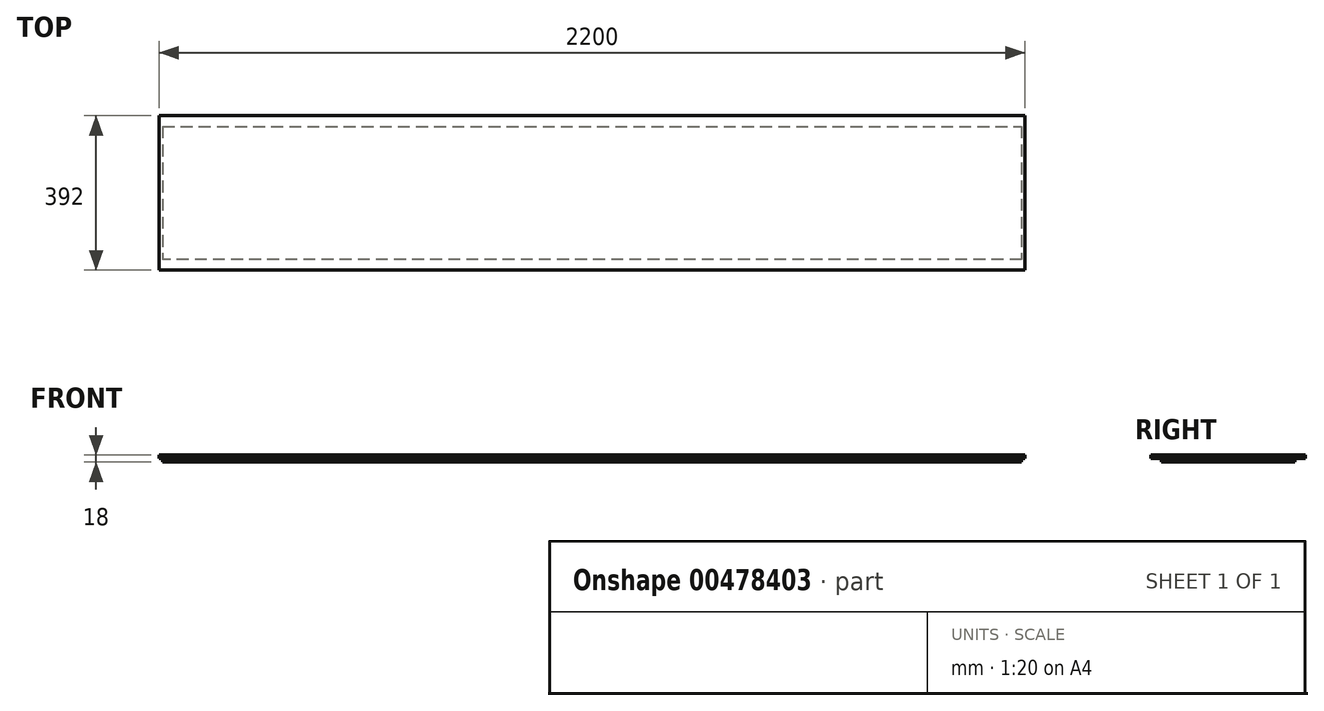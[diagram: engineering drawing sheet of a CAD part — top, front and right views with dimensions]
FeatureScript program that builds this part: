
annotation { "Feature Type Name" : "Feature", "Feature Type Description" : "" }
export const myFeature = defineFeature(function(context is Context, id is Id, definition is map)
    precondition{}
    {
        {
            var Q0;
            Q0=qCreatedBy(makeId("Top.planeOp"),FACE);
            var sketch = newSketch(context, id + "F0", { "sketchPlane" : qUnion([Q0])});
            skLineSegment(sketch, "E0.bottom", {"start": v(-966.15, 22.1) * mm, "end": v(133.85, 22.1) * mm});
            skPoint(sketch, "E1", {"position": v(133.85, 22.1) * mm});
            skPoint(sketch, "E2", {"position": v(-966.15, 22.1) * mm});
            skLineSegment(sketch, "E3.0", {"start": v(-966.15, -4.9) * mm, "end": v(133.85, -4.9) * mm});
            skLineSegment(sketch, "E4.0", {"start": v(-966.15, -369.9) * mm, "end": v(133.85, -369.9) * mm});
            skLineSegment(sketch, "E5", {"start": v(133.85, 22.1) * mm, "end": v(133.85, -369.9) * mm, "construction": true});
            skLineSegment(sketch, "E6", {"start": v(-966.15, 22.1) * mm, "end": v(-966.15, -369.9) * mm});
            skLineSegment(sketch, "E7.0", {"start": v(-957.15, 22.1) * mm, "end": v(-957.15, -369.9) * mm});
            skLineSegment(sketch, "E8.0", {"start": v(-966.15, -342.9) * mm, "end": v(133.85, -342.9) * mm});
            skLineSegment(sketch, "E9.MirrorCS", {"start": v(1233.85, 22.1) * mm, "end": v(1233.85, -369.9) * mm});
            skLineSegment(sketch, "E10.MirrorCS", {"start": v(1224.85, 22.1) * mm, "end": v(1224.85, -369.9) * mm});
            skPoint(sketch, "E11.MirrorP", {"position": v(1233.85, 22.1) * mm});
            skLineSegment(sketch, "E12.MirrorCS", {"start": v(1233.85, 22.1) * mm, "end": v(133.85, 22.1) * mm});
            skLineSegment(sketch, "E13.MirrorCS", {"start": v(1233.85, -4.9) * mm, "end": v(133.85, -4.9) * mm});
            skLineSegment(sketch, "E14.MirrorCS", {"start": v(1233.85, -342.9) * mm, "end": v(133.85, -342.9) * mm});
            skLineSegment(sketch, "E15.MirrorCS", {"start": v(1233.85, -369.9) * mm, "end": v(133.85, -369.9) * mm});
            skSolve(sketch);
        }
        {
            var Q0;
            Q0 = qSketchRegion(id + "F0", true);
            extrude(context, id + "F1", {"entities" : qUnion([Q0]), "depth" : -9 * mm});
        }
        {
            var Q0;
            {var subQ1=sQuery(id+"F0.wireOp",EDGE,"E3.0");var subQ5=sQuery(id+"F0.wireOp",EDGE,"E13.MirrorCS");var subQ11=makeQuery(id+"F0.imprint","INTERSECT",VERTEX,{"derivedFrom":[subQ1,subQ5]});Q0=makeQuery(id+"F0.imprint","IMPRINT",FACE,{"disambiguationData":[TD([[makeQuery(id+"F0.imprint","IMPRINT",EDGE,{"disambiguationData":[TD([[subQ11,1.0]])],"derivedFrom":subQ1}),-1.0]])]});}
            extrude(context, id + "F2", {"entities" : qUnion([Q0]), "operationType" : NewBodyOperationType.ADD, "depth" : -18 * mm});
        }
    });
